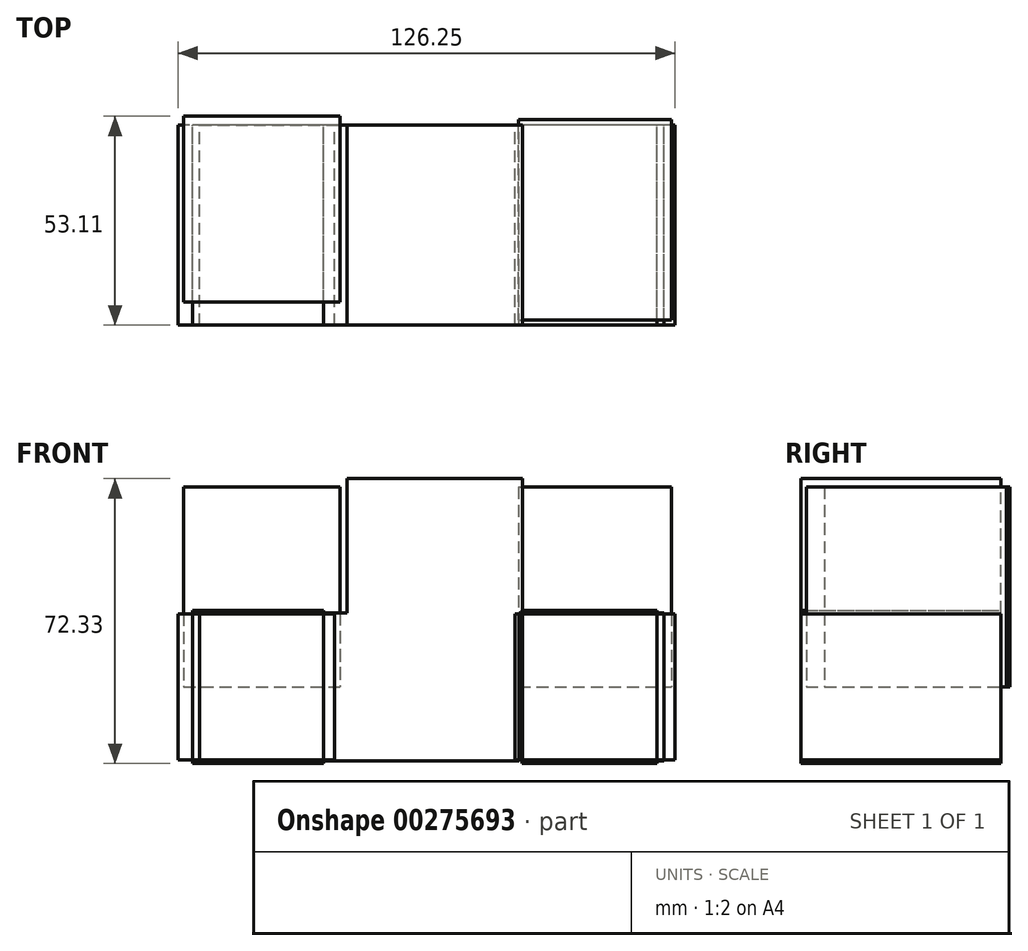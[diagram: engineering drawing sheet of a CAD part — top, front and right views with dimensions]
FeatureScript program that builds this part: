
annotation { "Feature Type Name" : "Feature", "Feature Type Description" : "" }
export const myFeature = defineFeature(function(context is Context, id is Id, definition is map)
    precondition{}
    {
        {
            var Q0;
            Q0=qCreatedBy(makeId("Front.planeOp"),FACE);
            var sketch = newSketch(context, id + "F0", { "sketchPlane" : qUnion([Q0])});
            skLineSegment(sketch, "E0.bottom", {"start": v(21.43, -18.84) * mm, "end": v(-21.43, -18.84) * mm});
            skLineSegment(sketch, "E0.top", {"start": v(21.43, 18.84) * mm, "end": v(-21.43, 18.84) * mm});
            skLineSegment(sketch, "E0.left", {"start": v(21.43, -18.84) * mm, "end": v(21.43, 18.84) * mm});
            skLineSegment(sketch, "E0.right", {"start": v(-21.43, -18.84) * mm, "end": v(-21.43, 18.84) * mm});
            skPoint(sketch, "E0.middle", {"position": v(0, 0) * mm});
            skLineSegment(sketch, "E1.bottom", {"start": v(58.16, -18.84) * mm, "end": v(22.3, -18.84) * mm});
            skLineSegment(sketch, "E1.top", {"start": v(58.16, 18.84) * mm, "end": v(22.3, 18.84) * mm});
            skLineSegment(sketch, "E1.left", {"start": v(58.16, -18.84) * mm, "end": v(58.16, 18.84) * mm});
            skLineSegment(sketch, "E1.right", {"start": v(22.3, -18.84) * mm, "end": v(22.3, 18.84) * mm});
            skPoint(sketch, "E1.middle", {"position": v(40.23, 0) * mm});
            skPoint(sketch, "E1.middle.positionSnap0", {"position": v(21.43, 0) * mm});
            skPoint(sketch, "E1.centerSnap0", {"position": v(21.43, 0) * mm});
            skLineSegment(sketch, "E2.bottom", {"start": v(-59.75, -18.84) * mm, "end": v(-20.64, -18.84) * mm});
            skLineSegment(sketch, "E2.top", {"start": v(-59.75, 18.84) * mm, "end": v(-20.64, 18.84) * mm});
            skLineSegment(sketch, "E2.left", {"start": v(-59.75, -18.84) * mm, "end": v(-59.75, 18.84) * mm});
            skLineSegment(sketch, "E2.right", {"start": v(-20.64, -18.84) * mm, "end": v(-20.64, 18.84) * mm});
            skPoint(sketch, "E2.middle", {"position": v(-40.2, 0) * mm});
            skLineSegment(sketch, "E3.bottom", {"start": v(22.3, 18.84) * mm, "end": v(-22.3, 18.84) * mm});
            skLineSegment(sketch, "E3.top", {"start": v(22.3, 52.91) * mm, "end": v(-22.3, 52.91) * mm});
            skLineSegment(sketch, "E3.left", {"start": v(22.3, 18.84) * mm, "end": v(22.3, 52.91) * mm});
            skLineSegment(sketch, "E3.right", {"start": v(-22.3, 18.84) * mm, "end": v(-22.3, 52.91) * mm});
            skPoint(sketch, "E3.middle", {"position": v(0, 35.88) * mm});
            skSolve(sketch);
        }
        {
            var Q0;
            Q0 = qSketchRegion(id + "F0", true);
            extrude(context, id + "F1", {"entities" : qUnion([Q0]), "depth" : 50.8 * mm});
        }
        {
            var Q0;
            Q0=qCreatedBy(makeId("Front.planeOp"),FACE);
            var sketch = newSketch(context, id + "F2", { "sketchPlane" : qUnion([Q0])});
            skLineSegment(sketch, "E4.bottom", {"start": v(-25.44, -18.5) * mm, "end": v(-65.2, -18.5) * mm});
            skLineSegment(sketch, "E4.top", {"start": v(-25.44, 18.5) * mm, "end": v(-65.2, 18.5) * mm});
            skLineSegment(sketch, "E4.left", {"start": v(-25.44, -18.5) * mm, "end": v(-25.44, 18.5) * mm});
            skLineSegment(sketch, "E4.right", {"start": v(-65.2, -18.5) * mm, "end": v(-65.2, 18.5) * mm});
            skPoint(sketch, "E4.middle", {"position": v(-45.32, 0) * mm});
            skLineSegment(sketch, "E5.bottom", {"start": v(61.04, -18.5) * mm, "end": v(20.35, -18.5) * mm});
            skLineSegment(sketch, "E5.top", {"start": v(61.04, 18.5) * mm, "end": v(20.35, 18.5) * mm});
            skLineSegment(sketch, "E5.left", {"start": v(61.04, -18.5) * mm, "end": v(61.04, 18.5) * mm});
            skLineSegment(sketch, "E5.right", {"start": v(20.35, -18.5) * mm, "end": v(20.35, 18.5) * mm});
            skPoint(sketch, "E5.middle", {"position": v(40.7, 0) * mm});
            skSolve(sketch);
        }
        {
            var Q0;
            Q0 = qSketchRegion(id + "F2", true);
            extrude(context, id + "F3", {"entities" : qUnion([Q0]), "depth" : 50.8 * mm});
        }
        {
            var Q0;
            Q0=qCreatedBy(makeId("Front.planeOp"),FACE);
            var sketch = newSketch(context, id + "F4", { "sketchPlane" : qUnion([Q0])});
            skLineSegment(sketch, "E6.bottom", {"start": v(-28.2, -19.42) * mm, "end": v(-61.5, -19.42) * mm});
            skLineSegment(sketch, "E6.top", {"start": v(-28.2, 19.42) * mm, "end": v(-61.5, 19.42) * mm});
            skLineSegment(sketch, "E6.left", {"start": v(-28.2, -19.42) * mm, "end": v(-28.2, 19.42) * mm});
            skLineSegment(sketch, "E6.right", {"start": v(-61.5, -19.42) * mm, "end": v(-61.5, 19.42) * mm});
            skPoint(sketch, "E6.middle", {"position": v(-44.86, 0) * mm});
            skLineSegment(sketch, "E7.bottom", {"start": v(56.42, -19.42) * mm, "end": v(22.2, -19.42) * mm});
            skLineSegment(sketch, "E7.top", {"start": v(56.42, 19.42) * mm, "end": v(22.2, 19.42) * mm});
            skLineSegment(sketch, "E7.left", {"start": v(56.42, -19.42) * mm, "end": v(56.42, 19.42) * mm});
            skLineSegment(sketch, "E7.right", {"start": v(22.2, -19.42) * mm, "end": v(22.2, 19.42) * mm});
            skPoint(sketch, "E7.middle", {"position": v(39.3, 0) * mm});
            skSolve(sketch);
        }
        {
            var Q0;
            Q0 = qSketchRegion(id + "F4", true);
            extrude(context, id + "F5", {"entities" : qUnion([Q0]), "depth" : 50.8 * mm});
        }
        {
            var Q0;
            Q0=qCreatedBy(makeId("Top.planeOp"),FACE);
            var sketch = newSketch(context, id + "F6", { "sketchPlane" : qUnion([Q0])});
            skLineSegment(sketch, "E8.bottom", {"start": v(21.27, -49.48) * mm, "end": v(60.12, -49.48) * mm});
            skLineSegment(sketch, "E8.top", {"start": v(21.27, 1.39) * mm, "end": v(60.12, 1.39) * mm});
            skLineSegment(sketch, "E8.left", {"start": v(21.27, -49.48) * mm, "end": v(21.27, 1.39) * mm});
            skLineSegment(sketch, "E8.right", {"start": v(60.12, -49.48) * mm, "end": v(60.12, 1.39) * mm});
            skPoint(sketch, "E8.middle", {"position": v(40.7, -24.05) * mm});
            skLineSegment(sketch, "E9.bottom", {"start": v(-63.82, -44.86) * mm, "end": v(-24.05, -44.86) * mm});
            skLineSegment(sketch, "E9.top", {"start": v(-63.82, 2.31) * mm, "end": v(-24.05, 2.31) * mm});
            skLineSegment(sketch, "E9.left", {"start": v(-63.82, -44.86) * mm, "end": v(-63.82, 2.31) * mm});
            skLineSegment(sketch, "E9.right", {"start": v(-24.05, -44.86) * mm, "end": v(-24.05, 2.31) * mm});
            skPoint(sketch, "E9.middle", {"position": v(-43.93, -21.27) * mm});
            skSolve(sketch);
        }
        {
            var Q0;
            Q0 = qSketchRegion(id + "F6", true);
            extrude(context, id + "F7", {"entities" : qUnion([Q0]), "depth" : 50.8 * mm});
        }
    });
